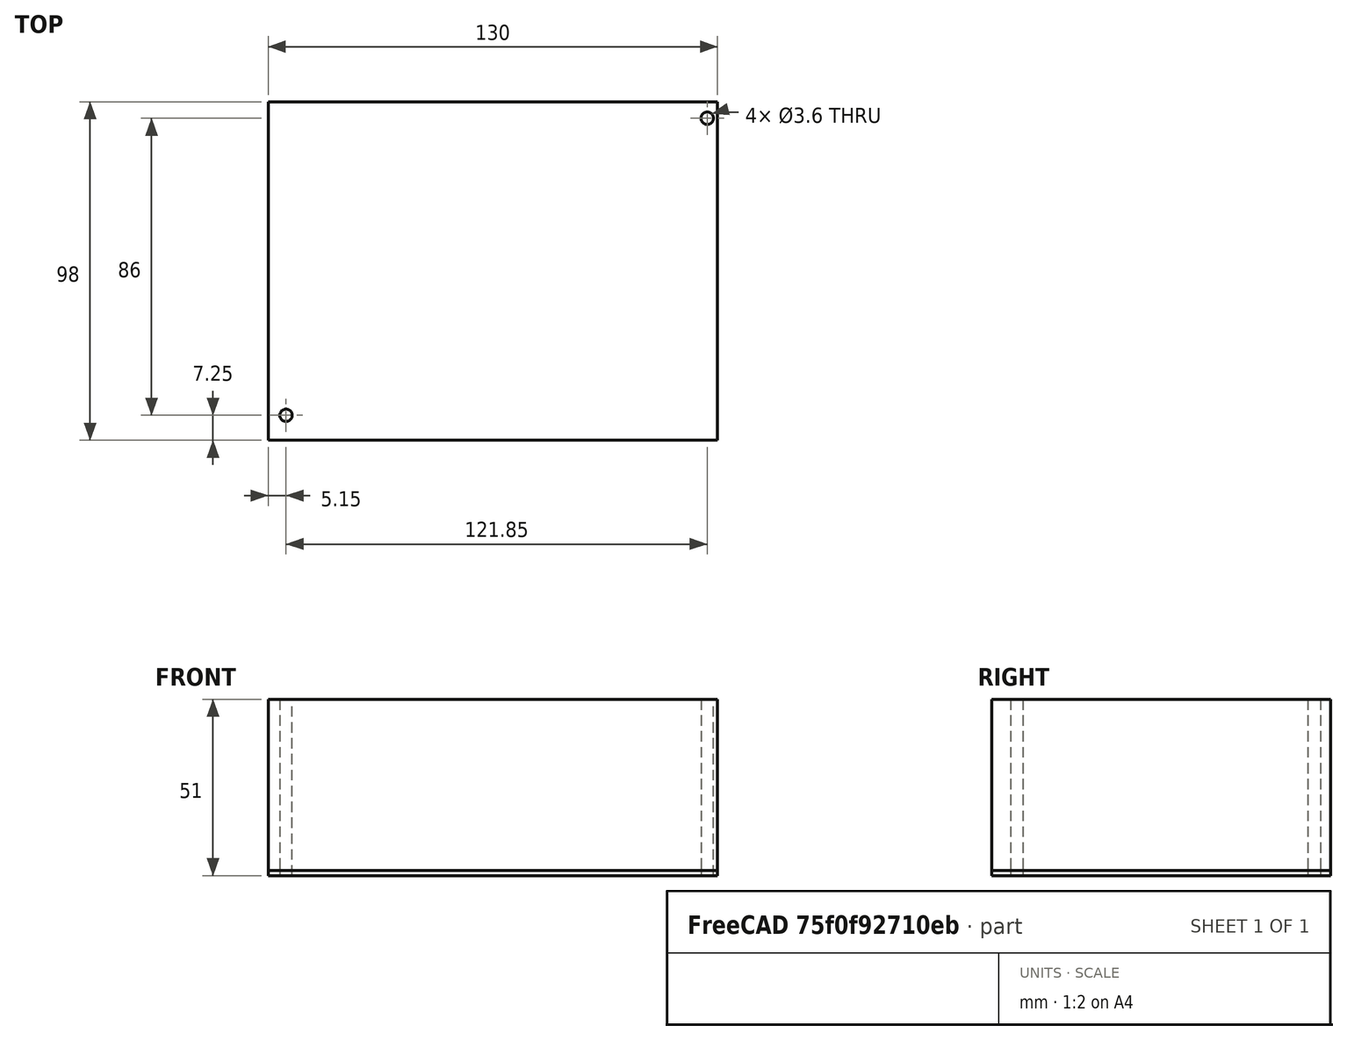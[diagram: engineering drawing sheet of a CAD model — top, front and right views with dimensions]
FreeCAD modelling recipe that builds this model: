
FCSTD DOCUMENT  (FreeCAD 0.19R23964 (Git))
Label: ps500wspindel
License: All rights reserved
LicenseURL: http://en.wikipedia.org/wiki/All_rights_reserved
objects: Part::Feature×2, Sketcher::SketchObject×1, PartDesign::Pad×1, PartDesign::Body×1
note: 6 computed .brp shape members not serialized (recipe doc carries the construction recipe); baked Part::Feature solids carry a one-line shape summary decoded from their .brp

FEATURE [Sketcher::SketchObject] Sketch
  FullyConstrained = true
  MapMode = 5
  Support = -> [XY_Plane]
  sketch-geometry (6):
    g0: LineSegment StartX=0 StartY=98 StartZ=0 EndX=130 EndY=98 EndZ=0
    g1: LineSegment StartX=130 StartY=98 StartZ=0 EndX=130 EndY=0 EndZ=0
    g2: LineSegment StartX=130 StartY=0 StartZ=0 EndX=0 EndY=0 EndZ=0
    g3: LineSegment StartX=0 StartY=0 StartZ=0 EndX=0 EndY=98 EndZ=0
    g4: Circle CenterX=127 CenterY=93.25 CenterZ=0 NormalX=0 NormalY=0 NormalZ=1 AngleXU=0 Radius=1.8
    g5: Circle CenterX=5.15 CenterY=7.25 CenterZ=0 NormalX=0 NormalY=0 NormalZ=1 AngleXU=0 Radius=1.8
  constraints (17):
    c: Coincident(g0,g1)
    c: Coincident(g1,g2)
    c: Coincident(g2,g3)
    c: Coincident(g3,g0)
    c: Horizontal(g0)
    c: Horizontal(g2)
    c: Vertical(g1)
    c: Vertical(g3)
    c: Coincident(g2,g-1)
    c: DistanceX(g0,g0) = 130
    c: DistanceY(g3,g3) = 98
    c: DistanceX(g2,g4) = 127
    c: DistanceY(g2,g4) = 93.25
    c: DistanceY(g2,g5) = 7.25
    c: DistanceX(g2,g5) = 5.15
    c: Radius(g5) = 1.8
    c: Equal(g5,g4)
FEATURE [PartDesign::Pad] Pad
  Direction = (1,1,1)
  Length = 1.5
  Length2 = 100
  Profile = -> Sketch
  Type = 0
FEATURE [PartDesign::Body] Body
  Group = -> [Sketch,Pad]
  Origin = -> Origin
  Tip = -> Pad
FEATURE [Part::Feature] Pad001  label="ps500wspindel_51"
  shape: bbox 130 x 98 x 51 mm, 8 faces (baked)
FEATURE [Part::Feature] Pad002  label="ps500wspindel_1.5"
  shape: bbox 130 x 98 x 1.5 mm, 8 faces (baked)
